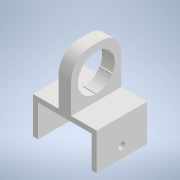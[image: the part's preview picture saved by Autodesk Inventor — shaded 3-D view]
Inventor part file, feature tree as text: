
AUTODESK INVENTOR PART (.ipt)
format: ipt  version: 2022 (Build 260153000, 153)  size: 174,080 bytes
history: native  units: mm
features: reference x6, other x5, extrude x3, sketch x3, fillet x1, projected_geometry x1
ambient origin geometry x8: Origin, YZ Plane, XZ Plane, XY Plane, X Axis, Y Axis, Z Axis, Center Point
bodies: Solid1 (feature_tree)
feature tree (19):
  extrude  "Extrusion1"  Depth=3.0mm
  extrude  "Extrusion2"  Depth=30.0mm
  extrude  "Extrusion3"  Depth=12.0mm
  fillet  "Fillet1"  Radius=30.0mm
  sketch  "Sketch2"  dims[d1=0.3mm d2=3.0mm]
  reference  "Reference9"
  reference  "Reference10"
  reference  "Reference11"
  reference  "Reference12"
  sketch  "Sketch3"  dims[d5=32.0mm d9=30.0mm]
  reference  "Reference13"
  reference  "Reference14"
  sketch  "Sketch4"  dims[d10=7.5mm d11=3.75mm d12=30.0mm d13=0.0mm d14=4.0mm d15=6.593302mm d16=60.0mm d17=0.0mm d18=0.3mm d19=3.0mm d20=22.0mm d21=1.0mm d22=60.0mm d24=360.0deg d26=10.0mm d27=0.0mm d28=12.0mm]
  projected_geometry  "Projected Loop1"
  other  "<userpath>\OneDrive\Escritorio\Mini_Proyecto_Diseno\Diseno_18012\Modelo_MPD\Carril.iam"
  other  "Carril.iam"
  other  "Base_Carril:1"
  other  "Lateral_Carril:2"
  other  "Lateral_Carril:1"
